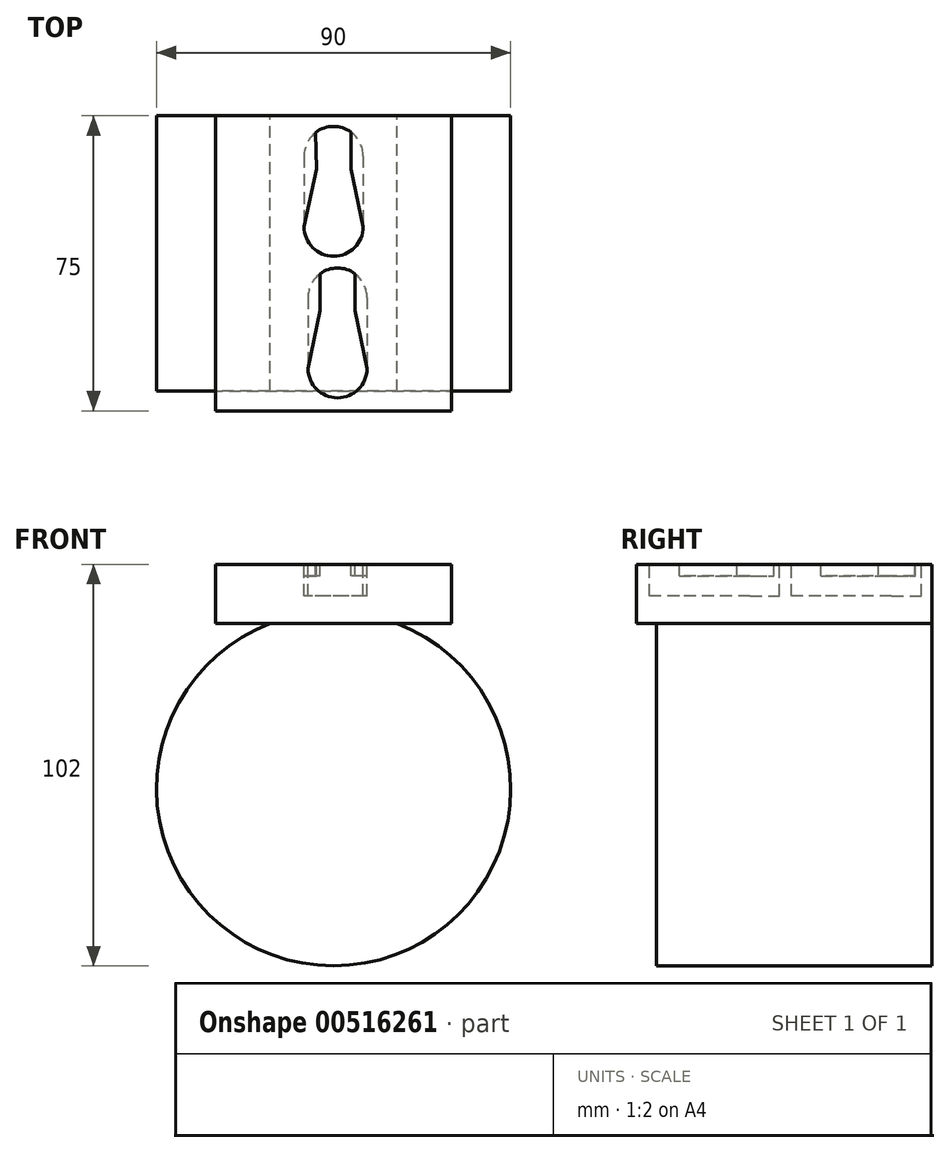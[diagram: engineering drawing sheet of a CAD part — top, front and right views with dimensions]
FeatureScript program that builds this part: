
annotation { "Feature Type Name" : "Feature", "Feature Type Description" : "" }
export const myFeature = defineFeature(function(context is Context, id is Id, definition is map)
    precondition{}
    {
        {
            var Q0;
            Q0=qCreatedBy(makeId("Front.planeOp"),FACE);
            var sketch = newSketch(context, id + "F0", { "sketchPlane" : qUnion([Q0])});
            skCircle(sketch, "E0", {"center": v(0, 0) * mm, "radius": 45 * mm});
            skSolve(sketch);
        }
        {
            var Q0;
            Q0=makeQuery(id+"F0.imprint","IMPRINT",FACE,{"disambiguationData":[TD([[makeQuery(id+"F0.imprint","IMPRINT",EDGE,{"derivedFrom":sQuery(id+"F0.wireOp",EDGE,"E0")}),1.0]])]});
            extrude(context, id + "F1", {"entities" : qUnion([Q0]), "depth" : 70 * mm, "offsetDistance" : 25 * mm});
        }
        {
            var Q0;
            Q0=qCreatedBy(makeId("Front.planeOp"),FACE);
            var sketch = newSketch(context, id + "F2", { "sketchPlane" : qUnion([Q0])});
            skLineSegment(sketch, "E1.bottom", {"start": v(-30, 57) * mm, "end": v(30, 57) * mm});
            skLineSegment(sketch, "E1.top", {"start": v(-30, 42) * mm, "end": v(30, 42) * mm});
            skLineSegment(sketch, "E1.left", {"start": v(-30, 57) * mm, "end": v(-30, 42) * mm});
            skLineSegment(sketch, "E1.right", {"start": v(30, 57) * mm, "end": v(30, 42) * mm});
            skSolve(sketch);
        }
        {
            var Q0;
            Q0=makeQuery(id+"F2.imprint","IMPRINT",FACE,{"disambiguationData":[TD([[makeQuery(id+"F2.imprint","IMPRINT",EDGE,{"derivedFrom":sQuery(id+"F2.wireOp",EDGE,"E1.bottom")}),-1.0]])]});
            extrude(context, id + "F3", {"entities" : qUnion([Q0]), "operationType" : NewBodyOperationType.ADD, "depth" : 75 * mm, "offsetDistance" : 25 * mm});
        }
        {
            var Q0;
            Q0=makeQuery(id+"F3.opExtrude","SWEPT_FACE",FACE,{"disambiguationData":[OSD([sQuery(id+"F2.wireOp",EDGE,"E1.bottom")])]});
            var sketch = newSketch(context, id + "F4", { "sketchPlane" : qUnion([Q0])});
            skLineSegment(sketch, "E2.bottom", {"start": v(-7.5, -10.22) * mm, "end": v(7.5, -10.22) * mm});
            skLineSegment(sketch, "E2.top", {"start": v(-7.5, -28.22) * mm, "end": v(7.5, -28.22) * mm});
            skLineSegment(sketch, "E2.left", {"start": v(-7.5, -10.22) * mm, "end": v(-7.5, -28.22) * mm});
            skLineSegment(sketch, "E2.right", {"start": v(7.5, -10.22) * mm, "end": v(7.5, -28.22) * mm});
            skLineSegment(sketch, "E3.bottom", {"start": v(-6.5, -46.2) * mm, "end": v(8.5, -46.2) * mm});
            skLineSegment(sketch, "E3.top", {"start": v(-6.5, -64.2) * mm, "end": v(8.5, -64.2) * mm});
            skLineSegment(sketch, "E3.left", {"start": v(-6.5, -46.2) * mm, "end": v(-6.5, -64.2) * mm});
            skLineSegment(sketch, "E3.right", {"start": v(8.5, -46.2) * mm, "end": v(8.5, -64.2) * mm});
            skCircle(sketch, "E4", {"center": v(0, -28.22) * mm, "radius": 7.5 * mm});
            skCircle(sketch, "E5", {"center": v(0, -10.22) * mm, "radius": 7.5 * mm});
            skCircle(sketch, "E6", {"center": v(1, -46.2) * mm, "radius": 7.5 * mm});
            skCircle(sketch, "E7", {"center": v(1, -64.2) * mm, "radius": 7.5 * mm});
            skSolve(sketch);
        }
        {
            var Q0;
            {var subQ0=sQuery(id+"F4.wireOp",EDGE,"E2.top");Q0=makeQuery(id+"F4.imprint","IMPRINT",FACE,{"disambiguationData":[TD([[makeQuery(id+"F4.imprint","IMPRINT",EDGE,{"derivedFrom":subQ0}),-1.0]])]});}
            var Q1;
            {var subQ0=sQuery(id+"F4.wireOp",EDGE,"E2.top");Q1=makeQuery(id+"F4.imprint","IMPRINT",FACE,{"disambiguationData":[TD([[makeQuery(id+"F4.imprint","IMPRINT",EDGE,{"derivedFrom":subQ0}),1.0]])]});}
            var Q2;
            Q2=makeQuery(id+"F4.imprint","IMPRINT",FACE,{"disambiguationData":[TD([[makeQuery(id+"F4.imprint","IMPRINT",EDGE,{"derivedFrom":sQuery(id+"F4.wireOp",EDGE,"E2.bottom")}),-1.0]])]});
            var Q3;
            Q3=makeQuery(id+"F4.imprint","IMPRINT",FACE,{"disambiguationData":[TD([[makeQuery(id+"F4.imprint","IMPRINT",EDGE,{"derivedFrom":sQuery(id+"F4.wireOp",EDGE,"E3.bottom")}),-1.0]])]});
            var Q4;
            {var subQ0=sQuery(id+"F4.wireOp",EDGE,"E3.top");Q4=makeQuery(id+"F4.imprint","IMPRINT",FACE,{"disambiguationData":[TD([[makeQuery(id+"F4.imprint","IMPRINT",EDGE,{"derivedFrom":subQ0}),1.0]])]});}
            var Q5;
            {var subQ0=sQuery(id+"F4.wireOp",EDGE,"E3.top");Q5=makeQuery(id+"F4.imprint","IMPRINT",FACE,{"disambiguationData":[TD([[makeQuery(id+"F4.imprint","IMPRINT",EDGE,{"derivedFrom":subQ0}),-1.0]])]});}
            var Q6;
            {var subQ0=sQuery(id+"F4.wireOp",EDGE,"E3.bottom");Q6=makeQuery(id+"F4.imprint","IMPRINT",FACE,{"disambiguationData":[TD([[makeQuery(id+"F4.imprint","IMPRINT",EDGE,{"derivedFrom":subQ0}),1.0]])]});}
            var Q7;
            {var subQ0=sQuery(id+"F4.wireOp",EDGE,"E2.bottom");Q7=makeQuery(id+"F4.imprint","IMPRINT",FACE,{"disambiguationData":[TD([[makeQuery(id+"F4.imprint","IMPRINT",EDGE,{"derivedFrom":subQ0}),1.0]])]});}
            var Q8;
            {var subQ0=sQuery(id+"F4.wireOp",EDGE,"E2.left");Q8=makeQuery(id+"F4.imprint","IMPRINT",FACE,{"disambiguationData":[TD([[makeQuery(id+"F4.imprint","IMPRINT",EDGE,{"derivedFrom":subQ0}),1.0]])]});}
            var Q9;
            {var subQ0=sQuery(id+"F4.wireOp",EDGE,"E3.left");Q9=makeQuery(id+"F4.imprint","IMPRINT",FACE,{"disambiguationData":[TD([[makeQuery(id+"F4.imprint","IMPRINT",EDGE,{"derivedFrom":subQ0}),1.0]])]});}
            extrude(context, id + "F5", {"entities" : qUnion([Q0, Q1, Q2, Q3, Q4, Q5, Q6, Q7, Q8, Q9]), "operationType" : NewBodyOperationType.REMOVE, "oppositeDirection" : true, "depth" : 8 * mm, "offsetDistance" : 25 * mm});
        }
        {
            var Q0;
            Q0=makeQuery(id+"F3.opExtrude","SWEPT_FACE",FACE,{"disambiguationData":[OSD([sQuery(id+"F2.wireOp",EDGE,"E1.bottom")])]});
            var sketch = newSketch(context, id + "F6", { "sketchPlane" : qUnion([Q0])});
            skPoint(sketch, "E8", {"position": v(0, -3.55) * mm});
            skLineSegment(sketch, "E9", {"start": v(-7.5, -28.22) * mm, "end": v(-4.39, -13.55) * mm});
            skLineSegment(sketch, "E10", {"start": v(-4.57, -2.72) * mm, "end": v(-7.5, -2.72) * mm});
            skLineSegment(sketch, "E11", {"start": v(-7.5, -2.72) * mm, "end": v(-7.5, -28.22) * mm});
            skLineSegment(sketch, "E12", {"start": v(7.5, -28.22) * mm, "end": v(4.39, -13.55) * mm});
            skLineSegment(sketch, "E13", {"start": v(4.39, -13.55) * mm, "end": v(4.39, -3.55) * mm});
            skLineSegment(sketch, "E14", {"start": v(4.39, -3.55) * mm, "end": v(7.5, -3.55) * mm});
            skLineSegment(sketch, "E15", {"start": v(7.5, -3.55) * mm, "end": v(7.5, -28.22) * mm});
            skLineSegment(sketch, "E16", {"start": v(8.5, -64.2) * mm, "end": v(5.5, -49.5) * mm});
            skLineSegment(sketch, "E17", {"start": v(5.5, -49.5) * mm, "end": v(5.5, -37.2) * mm});
            skLineSegment(sketch, "E18", {"start": v(5.5, -37.2) * mm, "end": v(8.5, -37.2) * mm});
            skLineSegment(sketch, "E19", {"start": v(8.5, -37.2) * mm, "end": v(8.5, -64.2) * mm});
            skLineSegment(sketch, "E20", {"start": v(-6.5, -64.2) * mm, "end": v(-6.5, -37.2) * mm});
            skLineSegment(sketch, "E21", {"start": v(-6.5, -37.2) * mm, "end": v(-3.5, -37.2) * mm});
            skLineSegment(sketch, "E22", {"start": v(-3.5, -37.2) * mm, "end": v(-3.5, -49.5) * mm});
            skLineSegment(sketch, "E23", {"start": v(-3.5, -49.5) * mm, "end": v(-6.5, -64.2) * mm});
            skLineSegment(sketch, "E24", {"start": v(-4.57, -2.72) * mm, "end": v(-4.39, -13.55) * mm});
            skSolve(sketch);
        }
        {
            var Q0;
            {var subQ0=sQuery(id+"F6.wireOp",EDGE,"E9");Q0=makeQuery(id+"F6.imprint","IMPRINT",FACE,{"disambiguationData":[TD([[makeQuery(id+"F6.imprint","IMPRINT",EDGE,{"derivedFrom":subQ0}),1.0]])]});}
            var Q1;
            {var subQ0=sQuery(id+"F6.wireOp",EDGE,"E12");Q1=makeQuery(id+"F6.imprint","IMPRINT",FACE,{"disambiguationData":[TD([[makeQuery(id+"F6.imprint","IMPRINT",EDGE,{"derivedFrom":subQ0}),-1.0]])]});}
            var Q2;
            {var subQ0=sQuery(id+"F6.wireOp",EDGE,"E16");Q2=makeQuery(id+"F6.imprint","IMPRINT",FACE,{"disambiguationData":[TD([[makeQuery(id+"F6.imprint","IMPRINT",EDGE,{"derivedFrom":subQ0}),-1.0]])]});}
            var Q3;
            {var subQ3=sQuery(id+"F6.wireOp",EDGE,"E23");Q3=makeQuery(id+"F6.imprint","IMPRINT",FACE,{"disambiguationData":[TD([[makeQuery(id+"F6.imprint","IMPRINT",EDGE,{"derivedFrom":subQ3}),-1.0]])]});}
            extrude(context, id + "F7", {"entities" : qUnion([Q0, Q1, Q2, Q3]), "operationType" : NewBodyOperationType.ADD, "oppositeDirection" : true, "depth" : 3 * mm, "offsetDistance" : 25 * mm});
        }
    });
